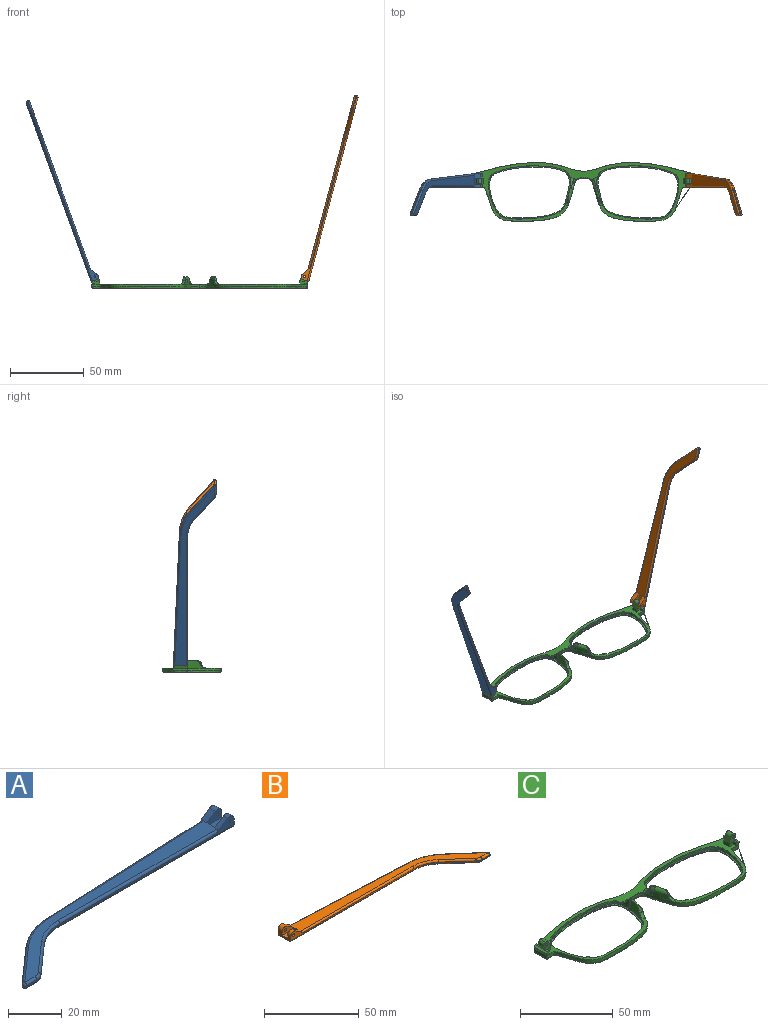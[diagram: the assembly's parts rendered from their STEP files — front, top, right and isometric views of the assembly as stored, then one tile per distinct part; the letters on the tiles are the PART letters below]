
ASSEMBLY  parts=3 mates=2
PART A: 43 faces, bbox 130.2x29.5x5.9 mm
  f0: plane 9.62x3.72mm, normal (1,0,0), area 24.7mm2, adj f1,f3,f4,f5,f10,f16,f18,f28
  f1: cylinder r=2.2mm len=3.45mm, axis (0,-1,0), area 11mm2, adj f0,f2,f4,f37
  f2: plane 6.01x3.91mm, normal (-0.55,0,0.84), area 12.7mm2, adj f1,f4,f9,f19,f37
  f3: plane 2.26x0.1mm, normal (0,0,1), area 0.1mm2, adj f0,f5,f18
  f4: plane 92.1x4.9mm, normal (0,-1,0), area 79.9mm2, adj f0,f1,f2,f14,f19,f36,f42
  f5: plane 93.42x4.13mm, normal (-0.04,1,0), area 64.8mm2, adj f0,f3,f11,f15,f17,f27,f28
  f6: plane 17.82x15.72mm, normal (-0.66,0.75,0), area 14.3mm2, adj f11,f12,f25,f30
  f7: plane 5.46x0.6mm, normal (0,-1,0), area 3.3mm2, adj f12,f13,f23,f32
  f8: plane 14.99x13.23mm, normal (0.66,-0.75,0), area 12mm2, adj f13,f14,f21,f34
  f9: plane 121.18x26.73mm, normal (0,0,1), area 627.7mm2, adj f2,f17,f19,f20,f21,f22,f23,f25
  f10: plane 129.1x27.08mm, normal (0,0,-1), area 686.5mm2, adj f0,f28,f29,f30,f32,f33,f34,f35
  f11: cylinder r=30mm len=18.52mm, axis (0,0,-1), area 12.2mm2, adj f5,f6,f26,f29
  f12: cylinder r=1mm len=1.75mm, axis (0,0,-1), area 1.5mm2, adj f6,f7,f24,f31
  f13: cylinder r=5mm len=3.31mm, axis (0,0,-1), area 2.2mm2, adj f7,f8,f22,f33
  f14: cylinder r=20mm len=13.23mm, axis (0,0,1), area 8.7mm2, adj f4,f8,f20,f35
  f15: plane 5.66x0.25mm, normal (0,0,-1), area 0.7mm2, adj f5,f17,f18
  f16: cylinder r=2.2mm len=3.45mm, axis (0,-1,0), area 14.8mm2, adj f0,f17,f18,f38
  f17: plane 6.01x3.91mm, normal (-0.55,0,0.84), area 16.9mm2, adj f5,f9,f15,f16,f18,f27,f38
  f18: plane 7.92x3.3mm, normal (0,1,0), area 15.9mm2, adj f0,f3,f15,f16,f17,f41
  f19: cylinder r=1mm len=84.18mm, axis (-1,0,0), area 131.4mm2, adj f2,f4,f9,f20
  f20: torus R=21mm, axis (0,0,1), area 23.1mm2, adj f9,f14,f19,f21
  f21: cylinder r=1mm len=15.65mm, axis (-0.75,-0.66,0), area 31.4mm2, adj f8,f9,f20,f22
  f22: torus R=4mm, axis (0,0,1), area 5.3mm2, adj f9,f13,f21,f23
  f23: cylinder r=1mm len=5.46mm, axis (-1,0,0), area 8.6mm2, adj f7,f9,f22,f24
  f24: sphere r=1mm, area 2.4mm2, adj f12,f23,f25
  f25: cylinder r=1mm len=18.48mm, axis (0.75,0.66,0), area 37.3mm2, adj f6,f9,f24,f26
  f26: torus R=29mm, axis (0,0,1), area 31.6mm2, adj f9,f11,f25,f27
  f27: cylinder r=1mm len=85.5mm, axis (1,0.04,0), area 133.5mm2, adj f5,f9,f17,f26
  f28: cylinder r=1mm len=93.46mm, axis (-1,-0.04,0), area 146.9mm2, adj f0,f5,f10,f29
  f29: torus R=29mm, axis (0,0,1), area 31.6mm2, adj f10,f11,f28,f30
  f30: cylinder r=1mm len=18.48mm, axis (-0.75,-0.66,0), area 37.3mm2, adj f6,f10,f29,f31
  f31: sphere r=1mm, area 2.4mm2, adj f12,f30,f32
  f32: cylinder r=1mm len=5.46mm, axis (1,0,0), area 8.6mm2, adj f7,f10,f31,f33
  f33: torus R=4mm, axis (0,0,1), area 5.3mm2, adj f10,f13,f32,f34
  f34: cylinder r=1mm len=15.65mm, axis (0.75,0.66,0), area 31.4mm2, adj f8,f10,f33,f35
  f35: torus R=21mm, axis (0,0,1), area 23.1mm2, adj f10,f14,f34,f36
  f36: cylinder r=1mm len=92.1mm, axis (1,0,0), area 144.7mm2, adj f0,f4,f10,f35
  f37: plane 7.92x4.7mm, normal (0,1,0), area 27mm2, adj f0,f1,f2,f39,f40,f42
  f38: plane 7.92x4.7mm, normal (0,-1,0), area 27mm2, adj f0,f16,f17,f39,f40,f41
  f39: plane 7.92x4.1mm, normal (0,0,1), area 32.5mm2, adj f0,f37,f38,f40
  f40: plane 4.1x1.4mm, normal (1,0,0), area 5.7mm2, adj f9,f37,f38,f39
  f41: cylinder r=0.5mm len=3.1mm, axis (0,-1,0), area 9.7mm2, adj f18,f38
  f42: cylinder r=0.5mm len=2.3mm, axis (0,-1,0), area 7.2mm2, adj f4,f37
PART B: 43 faces, bbox 130.2x29.5x5.9 mm
  f0: plane 9.62x3.72mm, normal (-1,0,0), area 24.7mm2, adj f1,f3,f4,f5,f10,f16,f18,f28
  f1: cylinder r=2.2mm len=3.45mm, axis (0,-1,0), area 11mm2, adj f0,f2,f4,f37
  f2: plane 6.01x3.91mm, normal (0.55,0,0.84), area 12.7mm2, adj f1,f4,f9,f19,f37
  f3: plane 2.26x0.1mm, normal (0,0,1), area 0.1mm2, adj f0,f5,f18
  f4: plane 92.1x4.9mm, normal (0,-1,0), area 78.2mm2, adj f0,f1,f2,f14,f19,f36,f42
  f5: plane 93.42x4.13mm, normal (0.04,1,0), area 64.8mm2, adj f0,f3,f11,f15,f17,f27,f28
  f6: plane 17.82x15.72mm, normal (0.66,0.75,0), area 14.3mm2, adj f11,f12,f25,f30
  f7: plane 5.46x0.6mm, normal (0,-1,0), area 3.3mm2, adj f12,f13,f23,f32
  f8: plane 14.99x13.23mm, normal (-0.66,-0.75,0), area 12mm2, adj f13,f14,f21,f34
  f9: plane 121.18x26.73mm, normal (0,0,1), area 627.7mm2, adj f2,f17,f19,f20,f21,f22,f23,f25
  f10: plane 129.1x27.08mm, normal (0,0,-1), area 686.5mm2, adj f0,f28,f29,f30,f32,f33,f34,f35
  f11: cylinder r=30mm len=18.52mm, axis (0,0,-1), area 12.2mm2, adj f5,f6,f26,f29
  f12: cylinder r=1mm len=1.75mm, axis (0,0,-1), area 1.5mm2, adj f6,f7,f24,f31
  f13: cylinder r=5mm len=3.31mm, axis (0,0,-1), area 2.2mm2, adj f7,f8,f22,f33
  f14: cylinder r=20mm len=13.23mm, axis (0,0,1), area 8.7mm2, adj f4,f8,f20,f35
  f15: plane 5.66x0.25mm, normal (0,0,-1), area 0.7mm2, adj f5,f17,f18
  f16: cylinder r=2.2mm len=3.45mm, axis (0,-1,0), area 14.8mm2, adj f0,f17,f18,f38
  f17: plane 6.01x3.91mm, normal (0.55,0,0.84), area 16.9mm2, adj f5,f9,f15,f16,f18,f27,f38
  f18: plane 7.92x3.3mm, normal (0,1,0), area 14.3mm2, adj f0,f3,f15,f16,f17,f41
  f19: cylinder r=1mm len=84.18mm, axis (1,0,0), area 131.4mm2, adj f2,f4,f9,f20
  f20: torus R=21mm, axis (0,0,1), area 23.1mm2, adj f9,f14,f19,f21
  f21: cylinder r=1mm len=15.65mm, axis (0.75,-0.66,0), area 31.4mm2, adj f8,f9,f20,f22
  f22: torus R=4mm, axis (0,0,1), area 5.3mm2, adj f9,f13,f21,f23
  f23: cylinder r=1mm len=5.46mm, axis (1,0,0), area 8.6mm2, adj f7,f9,f22,f24
  f24: sphere r=1mm, area 2.4mm2, adj f12,f23,f25
  f25: cylinder r=1mm len=18.48mm, axis (-0.75,0.66,0), area 37.3mm2, adj f6,f9,f24,f26
  f26: torus R=29mm, axis (0,0,1), area 31.6mm2, adj f9,f11,f25,f27
  f27: cylinder r=1mm len=85.5mm, axis (-1,0.04,0), area 133.5mm2, adj f5,f9,f17,f26
  f28: cylinder r=1mm len=93.46mm, axis (1,-0.04,0), area 146.9mm2, adj f0,f5,f10,f29
  f29: torus R=29mm, axis (0,0,1), area 31.6mm2, adj f10,f11,f28,f30
  f30: cylinder r=1mm len=18.48mm, axis (0.75,-0.66,0), area 37.3mm2, adj f6,f10,f29,f31
  f31: sphere r=1mm, area 2.4mm2, adj f12,f30,f32
  f32: cylinder r=1mm len=5.46mm, axis (-1,0,0), area 8.6mm2, adj f7,f10,f31,f33
  f33: torus R=4mm, axis (0,0,1), area 5.3mm2, adj f10,f13,f32,f34
  f34: cylinder r=1mm len=15.65mm, axis (-0.75,0.66,0), area 31.4mm2, adj f8,f10,f33,f35
  f35: torus R=21mm, axis (0,0,1), area 23.1mm2, adj f10,f14,f34,f36
  f36: cylinder r=1mm len=92.1mm, axis (-1,0,0), area 144.7mm2, adj f0,f4,f10,f35
  f37: plane 7.92x4.7mm, normal (0,1,0), area 25.4mm2, adj f0,f1,f2,f39,f40,f42
  f38: plane 7.92x4.7mm, normal (0,-1,0), area 25.4mm2, adj f0,f16,f17,f39,f40,f41
  f39: plane 7.92x4.1mm, normal (0,0,1), area 32.5mm2, adj f0,f37,f38,f40
  f40: plane 4.1x1.4mm, normal (-1,0,0), area 5.7mm2, adj f9,f37,f38,f39
  f41: cylinder r=0.88mm len=3.1mm, axis (0,-1,0), area 17mm2, adj f18,f38
  f42: cylinder r=0.88mm len=2.3mm, axis (0,-1,0), area 12.6mm2, adj f4,f37
PART C: 118 faces, bbox 148.1x40.9x10.5 mm
  f0: bspline ~1.82x1.22mm, area 0.7mm2, adj f1,f114,f116,f117
  f1: bspline ~2.66x2.04mm, area 1.9mm2, adj f0,f2,f113,f114,f117
  f2: bspline ~3.55x3.47mm, area 3.7mm2, adj f1,f3,f112,f113,f117
  f3: plane 147.73x40.49mm, normal (0,0,1), area 775.4mm2, adj f2,f4,f16,f17,f18,f19,f20,f21
  f4: plane 1.23x0.04mm, normal (0,0,1), area 0mm2, adj f3,f5,f114
  f5: plane 2.76x2.53mm, normal (0,-1,0), area 3.9mm2, adj f4,f6,f15,f16,f24
  f6: plane 9.65x1.24mm, normal (0,0,1), area 8.2mm2, adj f5,f7,f14,f15,f19,f20,f21,f24
  f7: plane 5.77x5.06mm, normal (0,-1,0), area 17mm2, adj f6,f8,f9,f11,f12,f13,f14,f23
  f8: cylinder r=1.98mm len=4mm, axis (0,-1,0), area 12.4mm2, adj f7,f12,f14,f21
  f9: plane 4x3.31mm, normal (-0.94,0,0.34), area 14.1mm2, adj f7,f10,f11,f21
  f10: plane 4x0.02mm, normal (0.34,0,0.94), area 0.1mm2, adj f9,f21,f22
  f11: cylinder r=1.98mm len=4mm, axis (0,1,0), area 12.4mm2, adj f7,f9,f12,f21
  f12: plane 4x0.01mm, normal (0.34,0,0.94), area 0mm2, adj f7,f8,f11,f21
  f13: cylinder r=0.88mm len=4mm, axis (0,-1,0), area 22mm2, adj f7,f21
  f14: plane 4x2.21mm, normal (0.94,0,-0.34), area 9.4mm2, adj f6,f7,f8,f21
  f15: plane 9.71x1.44mm, normal (0.34,0,0.94), area 13.9mm2, adj f5,f6,f16,f17,f18,f19
  f16: cone r=1mm half-angle=20deg, axis (0,0,1), area 2.3mm2, adj f3,f5,f15,f17
  f17: plane 7.67x1.6mm, normal (0.94,0,-0.34), area 13mm2, adj f3,f15,f16,f18
  f18: cylinder r=1mm len=2.28mm, axis (-0.34,0,-0.94), area 3mm2, adj f3,f15,f17,f19
  f19: plane 2.1x1.69mm, normal (0,1,0), area 2.8mm2, adj f3,f6,f15,f18,f20
  f20: plane 3.3x2.1mm, normal (-1,0,0), area 6.9mm2, adj f3,f6,f19,f21
  f21: plane 6.97x5.07mm, normal (0,1,0), area 22.7mm2, adj f3,f6,f8,f9,f10,f11,f12,f13
  f22: plane 4x2.36mm, normal (-1,0,0), area 9.5mm2, adj f3,f10,f21,f23
  f23: plane 3.2x2.36mm, normal (0,-1,0), area 5.7mm2, adj f3,f7,f22,f24
  f24: plane 2.35x2.1mm, normal (-1,0,0), area 4.9mm2, adj f3,f5,f6,f7,f23
  f25: bspline ~3.7x3.66mm, area 7.8mm2, adj f3,f26,f31,f39,f114
  f26: bspline ~7.26x7.26mm, area 6.3mm2, adj f25,f27,f31,f39
  f27: bspline ~10.29x4.84mm, area 21.4mm2, adj f26,f28,f31,f39,f114,f117
  f28: plane 3.62x0.97mm, normal (0,0,1), area 0.3mm2, adj f27,f29,f39
  f29: bspline ~8.14x4.16mm, area 6.4mm2, adj f28,f30,f39,f112,f117
  f30: extruded ~4.98x1.24mm, area 6mm2, adj f29,f39
  f31: extruded ~4.44x3.32mm, area 15.1mm2, adj f25,f26,f27,f32,f114
  f32: plane 4.46x1.45mm, normal (0,0,1), area 0.1mm2, adj f31,f114
  f33: cylinder r=1.3mm len=1.78mm, axis (0,0,1), area 1.3mm2, adj f3,f34,f39
  f34: plane 1.79x1.31mm, normal (0,0,-1), area 0.9mm2, adj f33,f39
  f35: cylinder r=1.3mm len=1.93mm, axis (0,0,1), area 1.5mm2, adj f3,f36,f39
  f36: plane 1.95x1.68mm, normal (0,0,-1), area 1.5mm2, adj f35,f39
  f37: cylinder r=2.28mm len=2.47mm, axis (0,0,1), area 1.7mm2, adj f3,f38,f39
  f38: plane 2.5x1.83mm, normal (0,0,-1), area 1.7mm2, adj f37,f39
  f39: extruded ~55.63x36.1mm, area 220.6mm2, adj f3,f25,f26,f27,f28,f29,f30,f33
  f40: extruded ~55.63x36.1mm, area 160.2mm2, adj f39,f41
  f41: plane 56.32x36.53mm, normal (0,0,1), area 124.9mm2, adj f40,f42
  f42: bspline ~56.15x36.68mm, area 237.6mm2, adj f41,f43
  f43: plane 144.78x37.85mm, normal (0,0,-1), area 478.1mm2, adj f42,f44,f47,f50,f51,f52,f53,f55
  f44: bspline ~56.15x36.68mm, area 237.6mm2, adj f43,f45
  f45: plane 56.32x36.53mm, normal (0,0,1), area 124.9mm2, adj f44,f46
  f46: extruded ~55.63x36.1mm, area 160.2mm2, adj f45,f86
  f47: bspline ~8.99x1.23mm, area 12.6mm2, adj f43,f48,f49,f114
  f48: bspline ~1x1mm, area 0.8mm2, adj f47,f58,f114
  f49: bspline ~1.04x1mm, area 0.7mm2, adj f47,f50,f114
  f50: bspline ~45.86x8.59mm, area 59.8mm2, adj f43,f49,f51,f114
  f51: bspline ~37.01x6.7mm, area 56.6mm2, adj f43,f50,f52,f111
  f52: bspline ~37.01x6.7mm, area 56.6mm2, adj f43,f51,f53,f110
  f53: bspline ~45.86x8.59mm, area 59.8mm2, adj f43,f52,f54,f109
  f54: bspline ~1.04x1mm, area 0.8mm2, adj f53,f55,f109
  f55: bspline ~8.99x1.23mm, area 12.6mm2, adj f43,f54,f56,f109
  f56: bspline ~1x1mm, area 0.8mm2, adj f55,f57,f109
  f57: bspline ~73.83x30.39mm, area 161.7mm2, adj f43,f56,f58,f109
  f58: bspline ~73.27x30.39mm, area 161.7mm2, adj f43,f48,f57,f114
  f59: plane 2.88x1.51mm, normal (0,0,-1), area 1.8mm2, adj f39,f60
  f60: cylinder r=2.28mm len=2.86mm, axis (0,0,1), area 1.8mm2, adj f3,f39,f59,f112
  f61: bspline ~6.38x2.14mm, area 2.6mm2, adj f3,f62,f113,f114
  f62: bspline ~6.38x2.14mm, area 2.6mm2, adj f3,f61,f63,f109
  f63: bspline ~1.82x1.13mm, area 0.6mm2, adj f62,f64,f76,f109
  f64: bspline ~2.65x2.03mm, area 1.9mm2, adj f63,f65,f68,f76,f109
  f65: bspline ~2.19x1.4mm, area 0.7mm2, adj f64,f66,f68,f109
  f66: extruded ~3.67x3.11mm, area 5.9mm2, adj f65,f67,f68,f109
  f67: bspline ~5.24x1.75mm, area 0mm2, adj f66,f109
  f68: bspline ~6.1x4.93mm, area 12.6mm2, adj f64,f65,f66,f69,f74,f76,f109
  f69: bspline ~10.29x4.84mm, area 21.5mm2, adj f68,f70,f71,f73,f86,f109
  f70: plane 3.62x0.97mm, normal (0,0,1), area 0.3mm2, adj f69,f74,f86
  f71: extruded ~4.44x3.32mm, area 15.1mm2, adj f69,f72,f73,f87,f109
  f72: plane 4.46x1.45mm, normal (0,0,1), area 0.1mm2, adj f71,f109
  f73: bspline ~7.26x7.26mm, area 6.2mm2, adj f69,f71,f86,f87
  f74: bspline ~8.14x4.16mm, area 6.4mm2, adj f68,f70,f75,f77,f86
  f75: extruded ~4.98x1.24mm, area 6mm2, adj f74,f86
  f76: bspline ~3.55x3.47mm, area 3.7mm2, adj f3,f63,f64,f68,f77
  f77: bspline ~5.94x4.42mm, area 7.6mm2, adj f3,f74,f76,f78,f86
  f78: cylinder r=2.28mm len=2.86mm, axis (0,0,1), area 1.8mm2, adj f3,f77,f79,f86
  f79: plane 2.88x1.51mm, normal (0,0,-1), area 1.8mm2, adj f78,f86
  f80: cylinder r=2.28mm len=2.47mm, axis (0,0,1), area 1.7mm2, adj f3,f81,f86
  f81: plane 2.5x1.83mm, normal (0,0,-1), area 1.7mm2, adj f80,f86
  f82: cylinder r=1.3mm len=1.93mm, axis (0,0,1), area 1.5mm2, adj f3,f83,f86
  f83: plane 1.95x1.68mm, normal (0,0,-1), area 1.5mm2, adj f82,f86
  f84: cylinder r=1.3mm len=1.78mm, axis (0,0,1), area 1.3mm2, adj f3,f85,f86
  f85: plane 1.79x1.31mm, normal (0,0,-1), area 0.9mm2, adj f84,f86
  f86: extruded ~55.63x36.1mm, area 220.6mm2, adj f3,f46,f69,f70,f73,f74,f75,f77
  f87: bspline ~3.7x3.66mm, area 7.8mm2, adj f3,f71,f73,f86,f109
  f88: plane 2.35x2.1mm, normal (1,0,0), area 4.9mm2, adj f3,f89,f91,f98,f100
  f89: plane 2.76x2.53mm, normal (0,-1,0), area 3.9mm2, adj f88,f90,f91,f107,f108
  f90: plane 9.71x1.44mm, normal (-0.34,0,0.94), area 13.9mm2, adj f89,f91,f104,f105,f106,f107
  f91: plane 9.65x1.24mm, normal (0,0,1), area 8.2mm2, adj f88,f89,f90,f92,f98,f102,f103,f104
  f92: plane 4x2.21mm, normal (-0.94,0,-0.34), area 9.4mm2, adj f91,f93,f98,f102
  f93: cylinder r=1.98mm len=4mm, axis (0,-1,0), area 12.4mm2, adj f92,f94,f98,f102
  f94: plane 4x0.01mm, normal (-0.34,0,0.94), area 0mm2, adj f93,f95,f98,f102
  f95: cylinder r=1.98mm len=4mm, axis (0,1,0), area 12.4mm2, adj f94,f96,f98,f102
  f96: plane 4x3.31mm, normal (0.94,0,0.34), area 14.1mm2, adj f95,f97,f98,f102
  f97: plane 4x0.02mm, normal (-0.34,0,0.94), area 0.1mm2, adj f96,f101,f102
  f98: plane 5.77x5.06mm, normal (0,-1,0), area 17mm2, adj f88,f91,f92,f93,f94,f95,f96,f99
  f99: cylinder r=0.88mm len=4mm, axis (0,-1,0), area 22mm2, adj f98,f102
  f100: plane 3.2x2.36mm, normal (0,-1,0), area 5.7mm2, adj f3,f88,f98,f101
  f101: plane 4x2.36mm, normal (1,0,0), area 9.5mm2, adj f3,f97,f100,f102
  f102: plane 6.97x5.07mm, normal (0,1,0), area 22.7mm2, adj f3,f91,f92,f93,f94,f95,f96,f97
  f103: plane 3.3x2.1mm, normal (1,0,0), area 6.9mm2, adj f3,f91,f102,f104
  f104: plane 2.1x1.69mm, normal (0,1,0), area 2.8mm2, adj f3,f90,f91,f103,f105
  f105: cylinder r=1mm len=2.28mm, axis (0.34,0,-0.94), area 3mm2, adj f3,f90,f104,f106
  f106: plane 7.67x1.6mm, normal (-0.94,0,-0.34), area 13mm2, adj f3,f90,f105,f107
  f107: cone r=1mm half-angle=20deg, axis (0,0,1), area 2.3mm2, adj f3,f89,f90,f106
  f108: plane 1.23x0.04mm, normal (0,0,1), area 0mm2, adj f3,f89,f109
  f109: extruded ~73.26x39.84mm, area 292.7mm2, adj f3,f53,f54,f55,f56,f57,f62,f63
  f110: extruded ~35.39x5.69mm, area 72.2mm2, adj f3,f52,f109,f111
  f111: extruded ~35.39x5.69mm, area 72.2mm2, adj f3,f51,f110,f114
  f112: bspline ~6.16x4.45mm, area 7.6mm2, adj f2,f3,f29,f39,f60
  f113: bspline ~1.82x1.13mm, area 0.6mm2, adj f1,f2,f61,f114
  f114: extruded ~73.26x39.84mm, area 292.7mm2, adj f0,f1,f3,f4,f25,f27,f31,f32
  f115: bspline ~5.24x1.75mm, area 0mm2, adj f114,f116
  f116: extruded ~3.67x3.11mm, area 5.9mm2, adj f0,f114,f115,f117
  f117: bspline ~6.1x4.93mm, area 12.7mm2, adj f0,f1,f2,f27,f29,f114,f116
PLACE A rot(axis=(0,1,0),70deg) t=(-84.77,-5.75,56)mm
PLACE B rot(axis=(0,-1,0),75deg) t=(68.2,-5.75,-61.61)mm
PLACE C t=(10.15,-1.13,-5.77)mm
MATE revolute A.f1 <-> C.f95  axis (0,-1,0) through (-60.89,2.72,1.22)mm
MATE revolute B.f41 <-> C.f8  axis (0,-1,0) through (81.2,2.72,1.21)mm
